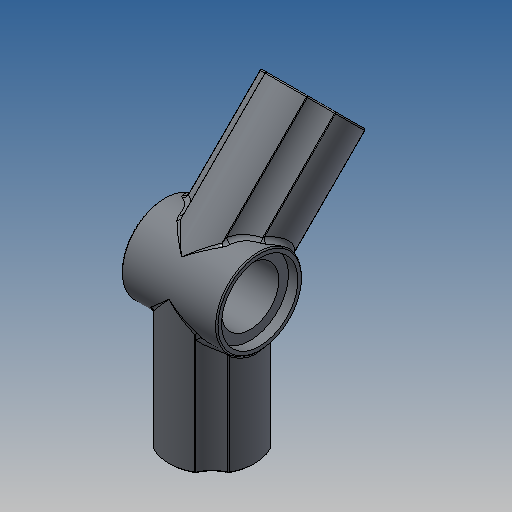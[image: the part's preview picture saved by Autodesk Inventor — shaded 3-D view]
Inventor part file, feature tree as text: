
AUTODESK INVENTOR PART (.ipt)
format: ipt  version: 2025 (Build 290162010, 162A)  size: 568,320 bytes
history: native  units: mm (DEFAULTED — no unit token found)
features: extrude x5, sketch x4, pattern_circular x1, hole x1, fillet x1, other x1
bodies: Solid1 (feature_tree)
feature tree (13):
  extrude  "Extrusion1"  Depth=7.2mm
  sketch  "Sketch20"  dims[d46=8.0mm d47=7.5mm d48=2.4mm d49=7.2mm d50=4.8mm d51=1.6mm d55=0.4mm d56=0.1mm d57=20.0mm d58=135.0deg d60=4.8mm d61=8.0mm d62=0.0mm d63=1.6mm d64=0.4mm d65=0.0mm]
  extrude  "Extrusion15"  Depth=0.8mm TaperAngle=0.0deg
  extrude  "Extrusion16"  Depth=0.1mm
  pattern_circular  "Circular Pattern1"  [2 undecoded]
  extrude  "Extrusion4"  Depth=0.1mm
  hole  "Hole1"  [1 undecoded]
  extrude  "Extrusion9"  Depth=0.1mm
  fillet  "Fillet1"  Radius=0.1mm
  other  "Origin Point"
  sketch  "Sketch6"  dims[d1=0.0mm d8=7.2mm]
  sketch  "Sketch12"  dims[d9=8.0mm d10=0.0mm]
  sketch  "Sketch13"  dims[d24=4.8mm d25=6.0mm d26=6.4mm d27=0.8mm d28=90.0deg d29=8.0mm d30=0.0mm d32=0.8mm d33=0.0mm]
note: 3 required parameter values undecoded (feature->parameter linkage not recoverable at this tier; creation-order binding heuristic only, values carry confidence <= 0.55)
